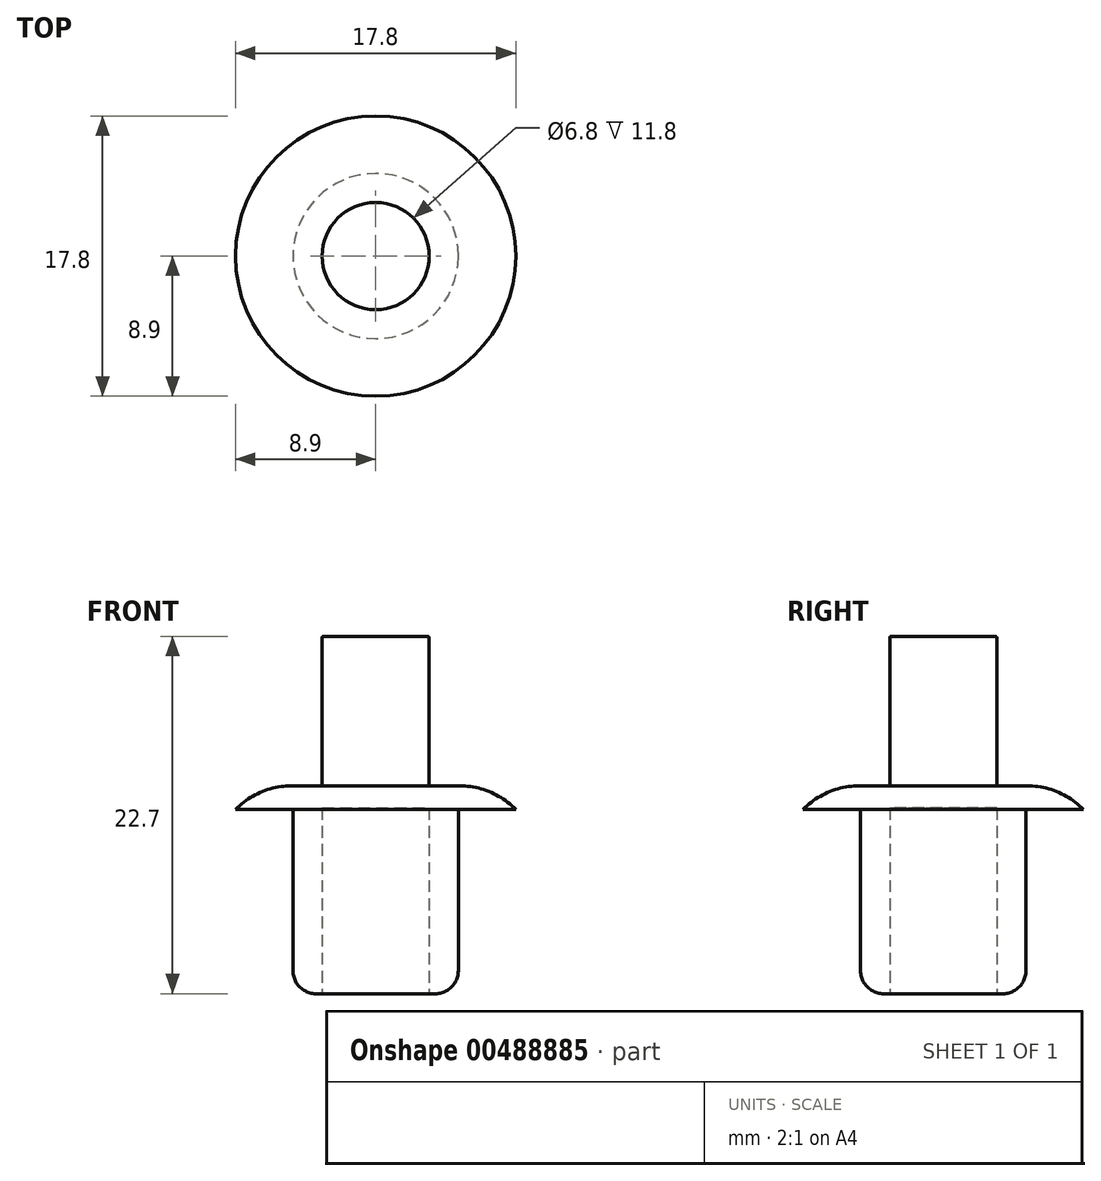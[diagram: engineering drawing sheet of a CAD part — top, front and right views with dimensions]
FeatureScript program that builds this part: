
annotation { "Feature Type Name" : "Feature", "Feature Type Description" : "" }
export const myFeature = defineFeature(function(context is Context, id is Id, definition is map)
    precondition{}
    {
        {
            var Q0;
            Q0=qCreatedBy(makeId("Top.planeOp"),FACE);
            var sketch = newSketch(context, id + "F0", { "sketchPlane" : qUnion([Q0])});
            skCircle(sketch, "E0", {"center": v(0, 0) * mm, "radius": 5.25 * mm});
            skSolve(sketch);
        }
        {
            var Q0;
            Q0=makeQuery(id+"F0.imprint","IMPRINT",FACE,{"disambiguationData":[TD([[makeQuery(id+"F0.imprint","IMPRINT",EDGE,{"derivedFrom":sQuery(id+"F0.wireOp",EDGE,"E0")}),1.0]])]});
            extrude(context, id + "F1", {"entities" : qUnion([Q0]), "depth" : 11.7 * mm});
        }
        {
            var Q0;
            Q0=makeQuery(id+"F1.opExtrude","CAP_FACE",FACE,{"disambiguationData":[OSD([sQuery(id+"F0.wireOp",EDGE,"E0")])],"isStart":false});
            var sketch = newSketch(context, id + "F2", { "sketchPlane" : qUnion([Q0])});
            skCircle(sketch, "E1", {"center": v(0, 0) * mm, "radius": 8.9 * mm});
            skSolve(sketch);
        }
        {
            var Q0;
            Q0 = qSketchRegion(id + "F2", true);
            extrude(context, id + "F3", {"entities" : qUnion([Q0]), "operationType" : NewBodyOperationType.ADD, "depth" : 1.5 * mm});
        }
        {
            var Q0;
            Q0=makeQuery(id+"F3.opExtrude","CAP_FACE",FACE,{"disambiguationData":[OSD([sQuery(id+"F2.wireOp",EDGE,"E1")])],"isStart":false});
            var sketch = newSketch(context, id + "F4", { "sketchPlane" : qUnion([Q0])});
            skCircle(sketch, "E2", {"center": v(0, 0) * mm, "radius": 3.4 * mm});
            skSolve(sketch);
        }
        {
            var Q0;
            Q0 = qSketchRegion(id + "F4", true);
            extrude(context, id + "F5", {"entities" : qUnion([Q0]), "operationType" : NewBodyOperationType.ADD, "depth" : 9.5 * mm});
        }
        {
            var Q0;
            Q0=makeQuery(id+"F3.opExtrude","CAP_EDGE",EDGE,{"disambiguationData":[OSD([sQuery(id+"F2.wireOp",EDGE,"E1")])],"isStart":false});
            fillet(context, id + "F6", {"entities" : qUnion([Q0]), "radius" : 5 * mm, "tangentPropagation" : true, "allowEdgeOverflow" : false});
        }
        {
            var Q0;
            Q0=makeQuery(id+"F5.opExtrude","SWEPT_FACE",FACE,{"disambiguationData":[OSD([sQuery(id+"F4.wireOp",EDGE,"E2")])]});
            fillet(context, id + "F7", {"entities" : qUnion([Q0]), "radius" : 0.1 * mm, "tangentPropagation" : true, "allowEdgeOverflow" : false});
        }
        {
            var Q0;
            Q0=makeQuery(id+"F1.opExtrude","CAP_FACE",FACE,{"disambiguationData":[OSD([sQuery(id+"F0.wireOp",EDGE,"E0")])],"isStart":true});
            var sketch = newSketch(context, id + "F8", { "sketchPlane" : qUnion([Q0])});
            skCircle(sketch, "E3", {"center": v(0, 0) * mm, "radius": 3.4 * mm});
            skSolve(sketch);
        }
        {
            var Q0;
            Q0 = qSketchRegion(id + "F8", true);
            extrude(context, id + "F9", {"entities" : qUnion([Q0]), "operationType" : NewBodyOperationType.REMOVE, "oppositeDirection" : true, "depth" : 11.8 * mm});
        }
        {
            var Q0;
            Q0=makeQuery(id+"F1.opExtrude","CAP_EDGE",EDGE,{"disambiguationData":[OSD([sQuery(id+"F0.wireOp",EDGE,"E0")])],"isStart":true});
            fillet(context, id + "F10", {"entities" : qUnion([Q0]), "radius" : 1.45 * mm, "tangentPropagation" : true, "allowEdgeOverflow" : false});
        }
    });
